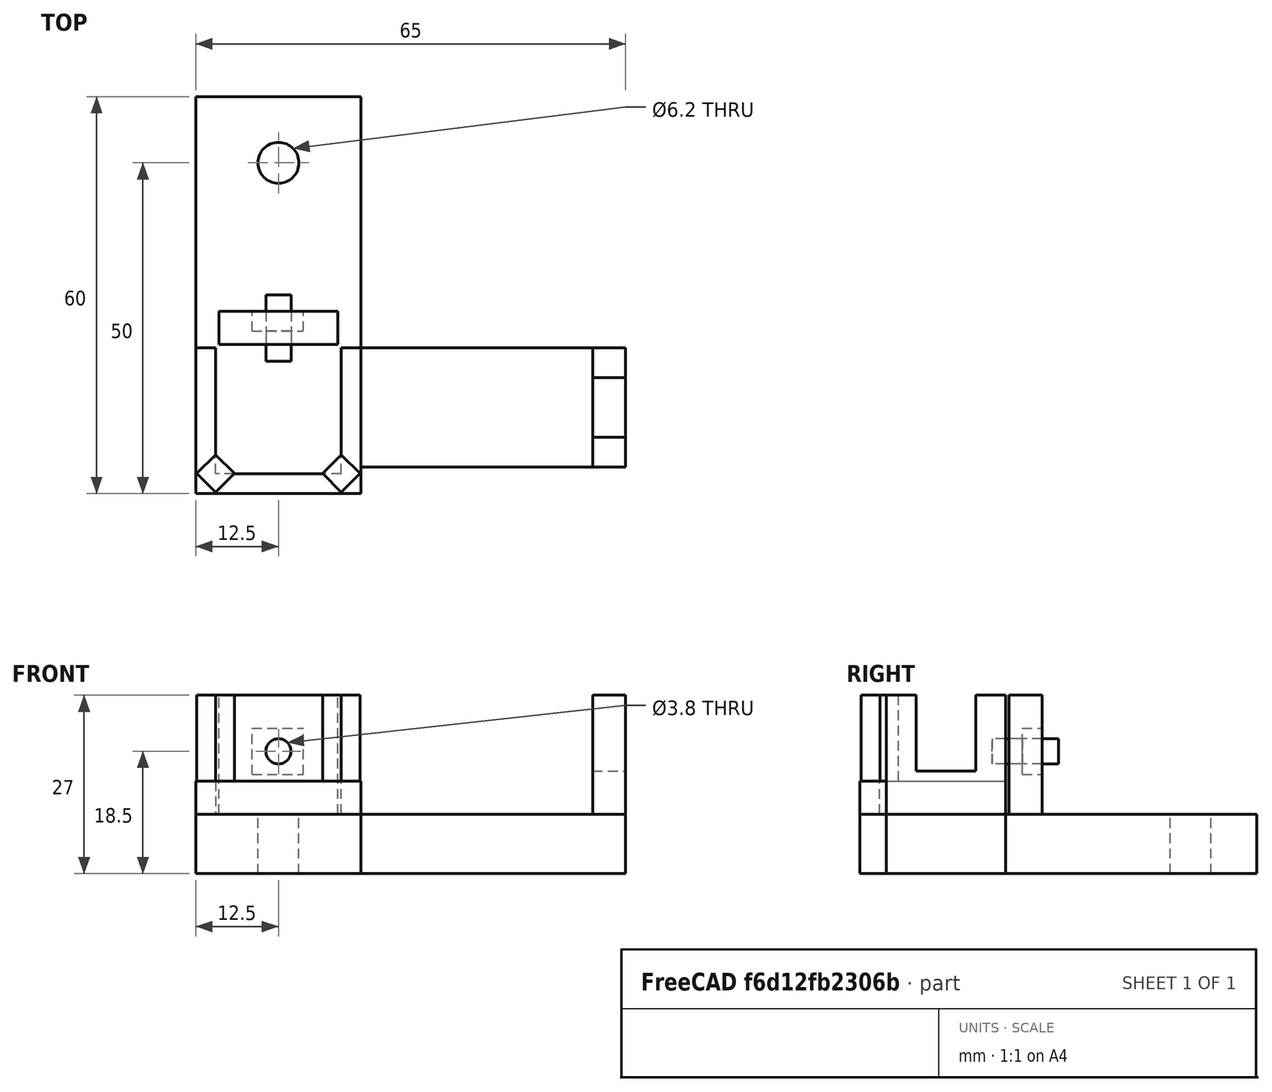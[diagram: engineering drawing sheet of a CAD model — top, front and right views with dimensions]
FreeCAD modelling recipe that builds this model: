
FCSTD DOCUMENT  (FreeCAD 0.18R16093 +53 (Git))
Label: HV_Plug_Valve_holder_4
License: All rights reserved
LicenseURL: http://en.wikipedia.org/wiki/All_rights_reserved
objects: Part::Box×10, Part::Cut×5, Part::Cylinder×3
note: 18 computed .brp shape members not serialized (recipe doc carries the construction recipe); baked Part::Feature solids carry a one-line shape summary decoded from their .brp

FEATURE [Part::Box] Box  label="Cube"
  AttacherType = Attacher::AttachEngine3D
  Height = 9
  Length = 25
  Width = 60
FEATURE [Part::Cylinder] Cylinder
  Angle = 360
  AttacherType = Attacher::AttachEngine3D
  Height = 15
  Placement = pos=(12.5,50,-3) rot=(0,0,1;0rad)
  Radius = 3.1
FEATURE [Part::Box] Box001  label="Cube001"
  AttacherType = Attacher::AttachEngine3D
  Height = 5
  Length = 25
  Placement = pos=(0,0,9) rot=(0,0,1;0rad)
  Width = 22
FEATURE [Part::Box] Box002  label="Cube002"
  AttacherType = Attacher::AttachEngine3D
  Height = 10
  Length = 19
  Placement = pos=(3,3,8) rot=(0,0,1;0rad)
  Width = 22
FEATURE [Part::Cut] Cut
  Base = -> Box001
  Tool = -> Box002
FEATURE [Part::Cut] Cut001
  Base = -> Box
  Tool = -> Cylinder
FEATURE [Part::Box] Box003  label="Cube003"
  AttacherType = Attacher::AttachEngine3D
  Height = 13
  Length = 4
  Placement = pos=(3,0.2,14) rot=(0,0,1;0.785398rad)
  Width = 4
FEATURE [Part::Box] Box004  label="Cube004"
  AttacherType = Attacher::AttachEngine3D
  Height = 13
  Length = 4
  Placement = pos=(22,0.2,14) rot=(0,0,1;0.785398rad)
  Width = 4
FEATURE [Part::Box] Box005  label="Cube005"
  AttacherType = Attacher::AttachEngine3D
  Height = 18
  Length = 18
  Placement = pos=(3.5,22.55,9) rot=(0,0,1;0rad)
  Width = 5
FEATURE [Part::Box] Box006  label="Cube006"
  AttacherType = Attacher::AttachEngine3D
  Height = 7
  Length = 7.8
  Placement = pos=(8.5,24.55,15) rot=(0,0,1;0rad)
  Width = 3
FEATURE [Part::Cylinder] Cylinder001
  Angle = 360
  AttacherType = Attacher::AttachEngine3D
  Height = 10
  Placement = pos=(12.5,30,18.5) rot=(1,0,0;1.5708rad)
  Radius = 1.9
FEATURE [Part::Cut] Cut002
  Base = -> Box005
  Tool = -> Box006
FEATURE [Part::Cut] Cut003
  Base = -> Cut002
  Tool = -> Cylinder001
FEATURE [Part::Cylinder] Cylinder002
  Angle = 360
  AttacherType = Attacher::AttachEngine3D
  Height = 10
  Placement = pos=(12.5,30,18.5) rot=(1,0,0;1.5708rad)
  Radius = 1.9
FEATURE [Part::Box] Box007  label="Cube007"
  AttacherType = Attacher::AttachEngine3D
  Height = 9
  Length = 40
  Placement = pos=(25,4,0) rot=(0,0,1;0rad)
  Width = 18
FEATURE [Part::Box] Box008  label="Cube008"
  AttacherType = Attacher::AttachEngine3D
  Height = 18
  Length = 5
  Placement = pos=(60,0,9) rot=(0,0,1;0rad)
  Width = 18
FEATURE [Part::Box] Box009  label="Cube009"
  AttacherType = Attacher::AttachEngine3D
  Height = 15
  Length = 10
  Placement = pos=(58,4.5,15.51) rot=(0,0,1;0rad)
  Width = 9
FEATURE [Part::Cut] Cut004
  Base = -> Box008
  Placement = pos=(0,4,0) rot=(0,0,1;0rad)
  Tool = -> Box009
